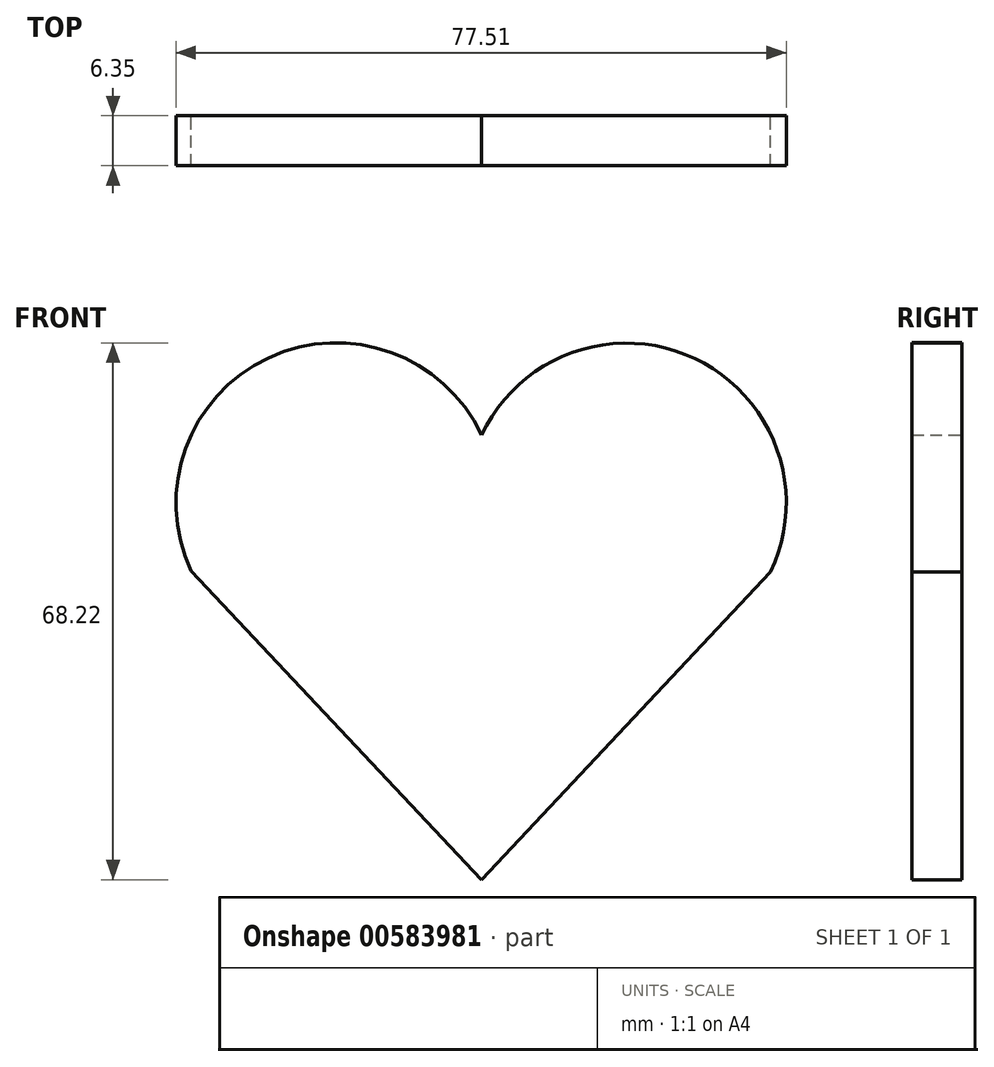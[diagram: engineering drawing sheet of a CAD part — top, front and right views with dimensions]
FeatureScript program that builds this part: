
annotation { "Feature Type Name" : "Feature", "Feature Type Description" : "" }
export const myFeature = defineFeature(function(context is Context, id is Id, definition is map)
    precondition{}
    {
        {
            var Q0;
            Q0=qCreatedBy(makeId("Front.planeOp"),FACE);
            var sketch = newSketch(context, id + "F0", { "sketchPlane" : qUnion([Q0])});
            skLineSegment(sketch, "E0", {"start": v(36.73, -17.4) * mm, "end": v(0, -56.5) * mm});
            skLineSegment(sketch, "E1", {"start": v(0, -56.5) * mm, "end": v(-36.87, -17.27) * mm});
            skArc(sketch, "E2", {"start": v(0, -17.27) * mm, "mid": v(-18.44, 11.72) * mm, "end": v(-36.87, -17.27) * mm});
            skArc(sketch, "E3", {"start": v(36.73, -17.4) * mm, "mid": v(18.46, 11.68) * mm, "end": v(0, -17.27) * mm});
            skSolve(sketch);
        }
        {
            var Q0;
            Q0 = qSketchRegion(id + "F0", true);
            extrude(context, id + "F1", {"entities" : qUnion([Q0]), "depth" : 6.35 * mm, "offsetDistance" : 25.4 * mm});
        }
    });
